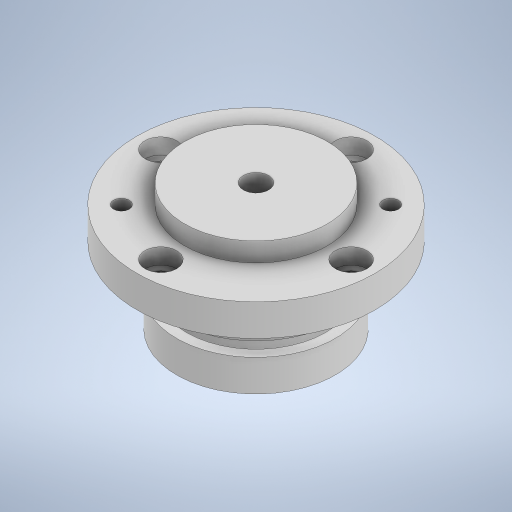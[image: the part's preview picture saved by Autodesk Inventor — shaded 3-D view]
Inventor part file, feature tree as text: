
AUTODESK INVENTOR PART (.ipt)
format: ipt  version: 2023 (Build 270158000, 158)  size: 304,640 bytes
history: native  units: mm
features: sketch x2, hole x2, revolve x1
ambient origin geometry x8: Origin, YZ Plane, XZ Plane, XY Plane, X Axis, Y Axis, Z Axis, Center Point
bodies: Solido1 (feature_tree)
feature tree (5):
  sketch  "Schizzo1"
  revolve  "Rivoluzione1"
  sketch  "Schizzo2"
  hole  "Foro1"  [1 undecoded]
  hole  "Foro2"  [1 undecoded]
note: 2 required parameter values undecoded (feature->parameter linkage not recoverable at this tier; creation-order binding heuristic only, values carry confidence <= 0.55)
